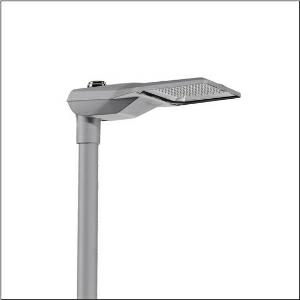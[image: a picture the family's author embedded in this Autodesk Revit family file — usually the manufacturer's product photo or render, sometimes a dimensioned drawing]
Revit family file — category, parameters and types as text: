
# Revit family: streetlight_sl_21_midi___st0_5a_5xe7b47n08mb_0aeb
name_source: partatom
category: Lighting Fixtures
units: mm (PartAtom-declared; Revit-internal decimal feet)

## family parameters
Cut with Voids When Loaded = No
Host = Face
Light Source = No
Part Type = Normal
Room Calculation Point = No
Round Connector Dimension = Use Diameter
Shared = No

## types (1)
- --- (1 x LED, 20180 lm, 147 W, 4000K)
    Apparent Load = 147 VA
    CIE Flux Codes = 41 75 97 100 100
    Color Rendering = 70
    Color Temperature = 4000K
    Default Elevation = 1800 mm
    Description = Streetlight SL 21 midi, mast luminaire, primary light control with lens, of PMMA, primary optical cover: cover, of toughened safety glass, transparent, light distribution: ST0.5a, light emission: direct distribution, primary light characteristic: asymmetric, installation type: side-entry, LED, 3G 2.5mm², High Power LED, rated luminous flux: 20.180lm, luminous efficacy: 137lm/W, light colour: 740, colour temperature: 4000K, control gear: NEMA (7pin), control: overheat protection, pre-setting: linear dimming characteristic, constant luminous flux control, time-dependent luminous flux control, flexible luminous flux parameterisation, mains connection: 220..240V, AC, 50/60Hz, connection cable pre-assembled, cable length: 12,5m, wiring characteristics: H05VV-F, start of lifetime: 147W, end of service life: 155W, reduction: 65W, luminaire housing, of diecast aluminium (EN AC-44300), powder-coated, SITECO metallic grey (DB 702S), corrosivity category C5 high according to DIN EN ISO 12944, multi-level sealing system, sealing non-destructively replaceable, inclination adjustable: 0°, 5°, 10°, 15°, length: 644mm, width: 335mm, height: 110mm, spigot size: 42mm (side-entry), mounting height: 4..8m, protection rating (complete): IP66, insulation class (complete): insulation class I (protective earthing), certification: CE, ENEC, ENEC+, VDE, impact resistance: IK10, permissible operating ambient temperature for outdoor applications: -40..+50°C, standard-compliant lighting for roads and squares, packaging unit: 1 piece

Light Distribution: ST0.5a
    Height = 111 mm
    Lamp = 1 x LED
    Lamp Light Flux = 20180 lm
    Lamp Power = 147 W
    Lamp count = 1
    Length = 644 mm
    Luminous efficacy = 137 lm/W
    Manufacturer = Siteco
    ModVariant = No
    Model = 5XE7B47N08MB
    Number of Poles = 1
    OnlyDefault = Yes
    Power Factor = 1
    Product Name = Streetlight SL 21 midi | ST0.5a
    Product group = mast luminaire | pylon top
    ProductGroupID = 6100
    Protection Class = Protection class I
    Protection Degree = IP 66
    RLX_Detail_Level = 1
    RLX_Emergency_Light_Flux = 0 lm
    RLX_Emergency_Type = 0
    RLX_Emergency_Type_DB = No
    RlxData = <blob elided: 37509 chars, md5=656dea69>
    Socket = socket
    Standby Power = 0 W
    System Light Flux = 20180 lm
    System Power = 147 W
    Type Comments = factory setting: luminous flux: 100 % | dim-lin: 254 | 750 mA
    Type Image = l_1294377.jpg
    URL = http://relux.com
    VarID = @adj_136757
    Voltage = 0 V
    Weight = 0.00 kg
    Width = 336 mm

## geometry (parser evidence)
native form markers: Blend x4, Sweep x11
no freeform markers — native parametric forms only
